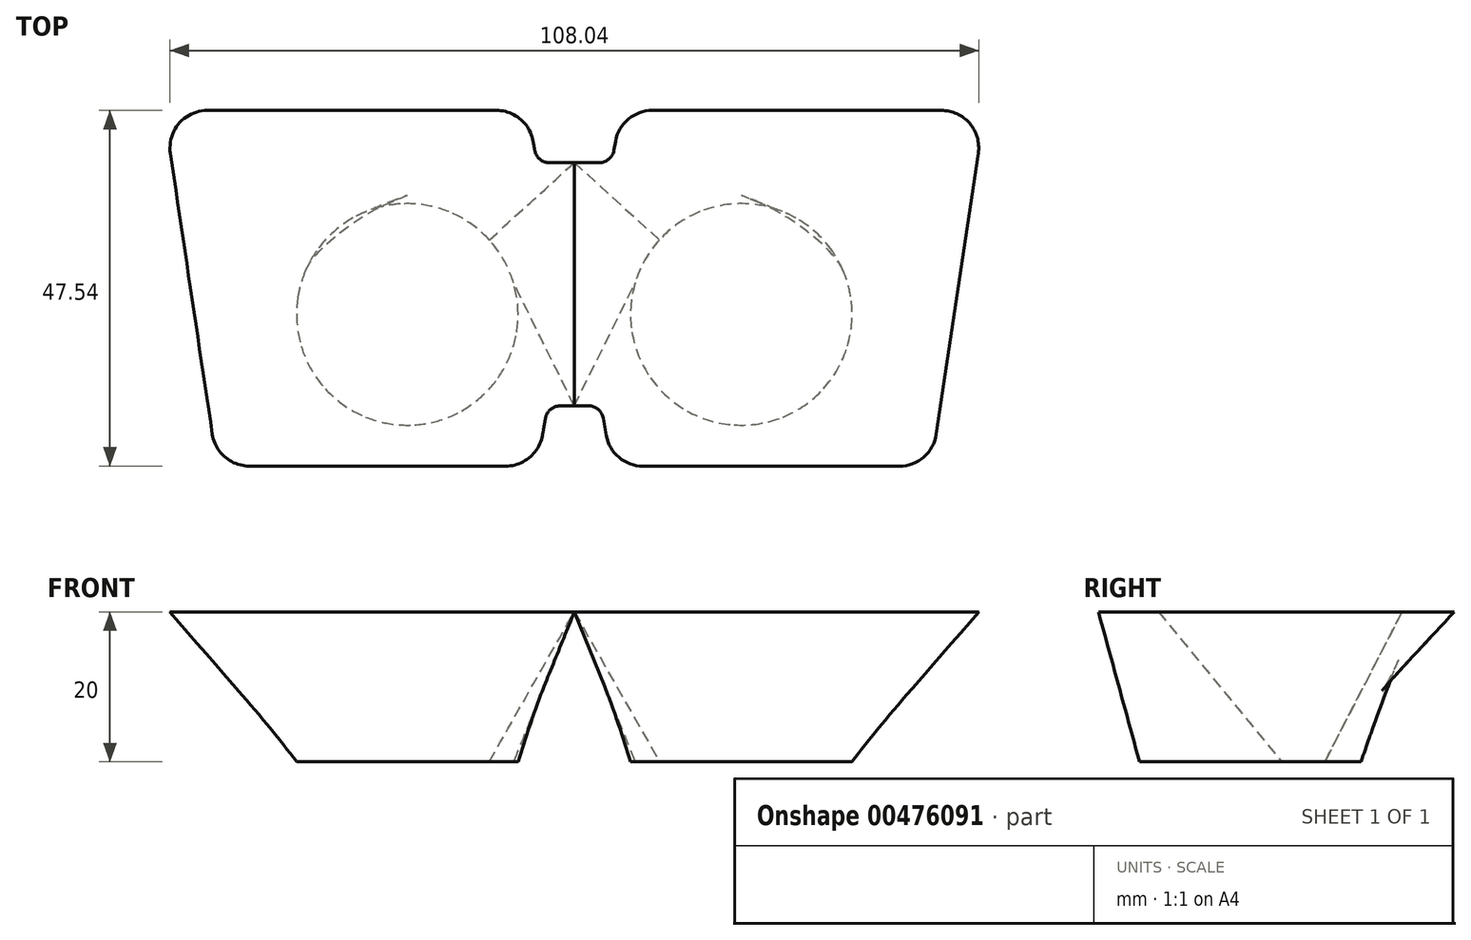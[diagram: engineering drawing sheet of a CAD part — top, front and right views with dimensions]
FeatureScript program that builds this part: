
annotation { "Feature Type Name" : "Feature", "Feature Type Description" : "" }
export const myFeature = defineFeature(function(context is Context, id is Id, definition is map)
    precondition{}
    {
        {
            var Q0;
            Q0=qCreatedBy(makeId("Top.planeOp"),FACE);
            var sketch = newSketch(context, id + "F0", { "sketchPlane" : qUnion([Q0])});
            skLineSegment(sketch, "E0.bottom", {"start": v(-65.28, 70.79) * mm, "end": v(65.28, 70.79) * mm});
            skLineSegment(sketch, "E0.top", {"start": v(-65.28, -70.79) * mm, "end": v(65.28, -70.79) * mm});
            skLineSegment(sketch, "E0.left", {"start": v(-65.28, 70.79) * mm, "end": v(-65.28, -70.79) * mm});
            skLineSegment(sketch, "E0.right", {"start": v(65.28, 70.79) * mm, "end": v(65.28, -70.79) * mm});
            skLineSegment(sketch, "E1", {"start": v(0, 0) * mm, "end": v(-65.28, 0) * mm, "construction": true});
            skLineSegment(sketch, "E2", {"start": v(0, 0) * mm, "end": v(65.28, 0) * mm, "construction": true});
            skCircle(sketch, "E3", {"center": v(28.29, -39.01) * mm, "radius": 18.72 * mm, "construction": true});
            skLineSegment(sketch, "E4", {"start": v(0, 70.79) * mm, "end": v(0, 0) * mm, "construction": true});
            skLineSegment(sketch, "E5", {"start": v(0, -39.01) * mm, "end": v(28.29, -39.01) * mm, "construction": true});
            skLineSegment(sketch, "E6", {"start": v(0, -18.73) * mm, "end": v(3.32, -18.73) * mm});
            skLineSegment(sketch, "E7", {"start": v(5.29, -17.09) * mm, "end": v(5.5, -15.86) * mm});
            skLineSegment(sketch, "E8", {"start": v(10.43, -11.75) * mm, "end": v(49.02, -11.75) * mm});
            skLineSegment(sketch, "E9", {"start": v(53.97, -17.48) * mm, "end": v(48.36, -55.03) * mm});
            skLineSegment(sketch, "E10", {"start": v(43.42, -59.3) * mm, "end": v(9.18, -59.3) * mm});
            skLineSegment(sketch, "E11", {"start": v(4.26, -55.17) * mm, "end": v(3.85, -52.88) * mm});
            skLineSegment(sketch, "E12", {"start": v(1.88, -51.23) * mm, "end": v(0, -51.23) * mm});
            skPoint(sketch, "E13.orphan", {"position": v(0, -39.01) * mm});
            skPoint(sketch, "E14.start.orphan", {"position": v(0, -70.79) * mm});
            skLineSegment(sketch, "E15", {"start": v(0, -70.79) * mm, "end": v(0, -51.23) * mm, "construction": true});
            skLineSegment(sketch, "E16", {"start": v(0, 0) * mm, "end": v(0, -18.73) * mm, "construction": true});
            skPoint(sketch, "E17.visualSharp", {"position": v(6.25, -11.75) * mm});
            skArc(sketch, "E17.filletArc", {"start": v(10.43, -11.75) * mm, "mid": v(7.22, -12.91) * mm, "end": v(5.5, -15.86) * mm});
            skPoint(sketch, "E18.visualSharp", {"position": v(54.82, -11.75) * mm});
            skArc(sketch, "E18.filletArc", {"start": v(53.97, -17.48) * mm, "mid": v(52.8, -13.48) * mm, "end": v(49.02, -11.75) * mm});
            skPoint(sketch, "E19.visualSharp", {"position": v(47.72, -59.3) * mm});
            skArc(sketch, "E19.filletArc", {"start": v(43.42, -59.3) * mm, "mid": v(46.68, -58.08) * mm, "end": v(48.36, -55.03) * mm});
            skPoint(sketch, "E20.visualSharp", {"position": v(5, -59.3) * mm});
            skArc(sketch, "E20.filletArc", {"start": v(4.26, -55.17) * mm, "mid": v(5.97, -58.13) * mm, "end": v(9.18, -59.3) * mm});
            skLineSegment(sketch, "E21", {"start": v(3.55, -51.23) * mm, "end": v(1.37, -39.01) * mm, "construction": true});
            skLineSegment(sketch, "E22", {"start": v(1.37, -39.01) * mm, "end": v(5, -18.73) * mm, "construction": true});
            skPoint(sketch, "E23.visualSharp", {"position": v(-65.28, -70.79) * mm});
            skPoint(sketch, "E24.visualSharp", {"position": v(5, -18.73) * mm});
            skArc(sketch, "E24.filletArc", {"start": v(3.32, -18.73) * mm, "mid": v(4.6, -18.27) * mm, "end": v(5.29, -17.09) * mm});
            skPoint(sketch, "E25.visualSharp", {"position": v(3.55, -51.23) * mm});
            skArc(sketch, "E25.filletArc", {"start": v(3.85, -52.88) * mm, "mid": v(3.16, -51.7) * mm, "end": v(1.88, -51.23) * mm});
            skPoint(sketch, "E26.MirrorCS.end.orphan", {"position": v(0, -51.23) * mm});
            skPoint(sketch, "E27.MirrorCS.start.orphan", {"position": v(0, -18.73) * mm});
            skLineSegment(sketch, "E28", {"start": v(0, -18.73) * mm, "end": v(0, -51.23) * mm});
            skSolve(sketch);
        }
        {
            var Q0;
            Q0=qCreatedBy(makeId("Top.planeOp"),FACE);
            cPlane(context, id + "F1", {"entities" : qUnion([Q0]), "cplaneType" : CPlaneType.OFFSET, "offset" : 20 * mm, "oppositeDirection" : true, "width" : 150 * mm, "height" : 150 * mm});
        }
        {
            var Q0;
            Q0=qCreatedBy(id+"F1.planeOp",FACE);
            var sketch = newSketch(context, id + "F2", { "sketchPlane" : qUnion([Q0])});
            skCircle(sketch, "E29.0", {"center": v(22.31, -39.01) * mm, "radius": 14.8 * mm});
            skLineSegment(sketch, "E30.0", {"start": v(0, 0) * mm, "end": v(0, -18.73) * mm, "construction": true});
            skSolve(sketch);
        }
        {
            var Q0;
            Q0=makeQuery(id+"F0.imprint","IMPRINT",FACE,{"disambiguationData":[TD([[makeQuery(id+"F0.imprint","IMPRINT",EDGE,{"derivedFrom":sQuery(id+"F0.wireOp",EDGE,"E6")}),-1.0]])]});
            var Q1;
            Q1 = qSketchRegion(id + "F2", true);
            loft(context, id + "F3", {"sheetProfilesArray" : [{ "sheetProfileEntities" : qUnion([Q0]) }, { "sheetProfileEntities" : qUnion([Q1]) }]});
        }
        {
            var Q0;
            Q0=makeQuery(id+"F3.opLoft","SWEPT_BODY",BODY,{"disambiguationData":[OSD([makeQuery(id+"F0.imprint","IMPRINT",FACE,{"disambiguationData":[TD([[makeQuery(id+"F0.imprint","IMPRINT",EDGE,{"derivedFrom":sQuery(id+"F0.wireOp",EDGE,"E6")}),-1.0]])]}),makeQuery(id+"F2.imprint","IMPRINT",FACE,{"disambiguationData":[TD([[makeQuery(id+"F2.imprint","IMPRINT",EDGE,{"derivedFrom":sQuery(id+"F2.wireOp",EDGE,"E29.0")}),1.0]])]})])]});
            var Q1;
            Q1=qCreatedBy(makeId("Right.planeOp"),FACE);
            mirror(context, id + "F4", {"operationType" : NewBodyOperationType.ADD, "entities" : qUnion([Q0]), "mirrorPlane" : qUnion([Q1])});
        }
    });
